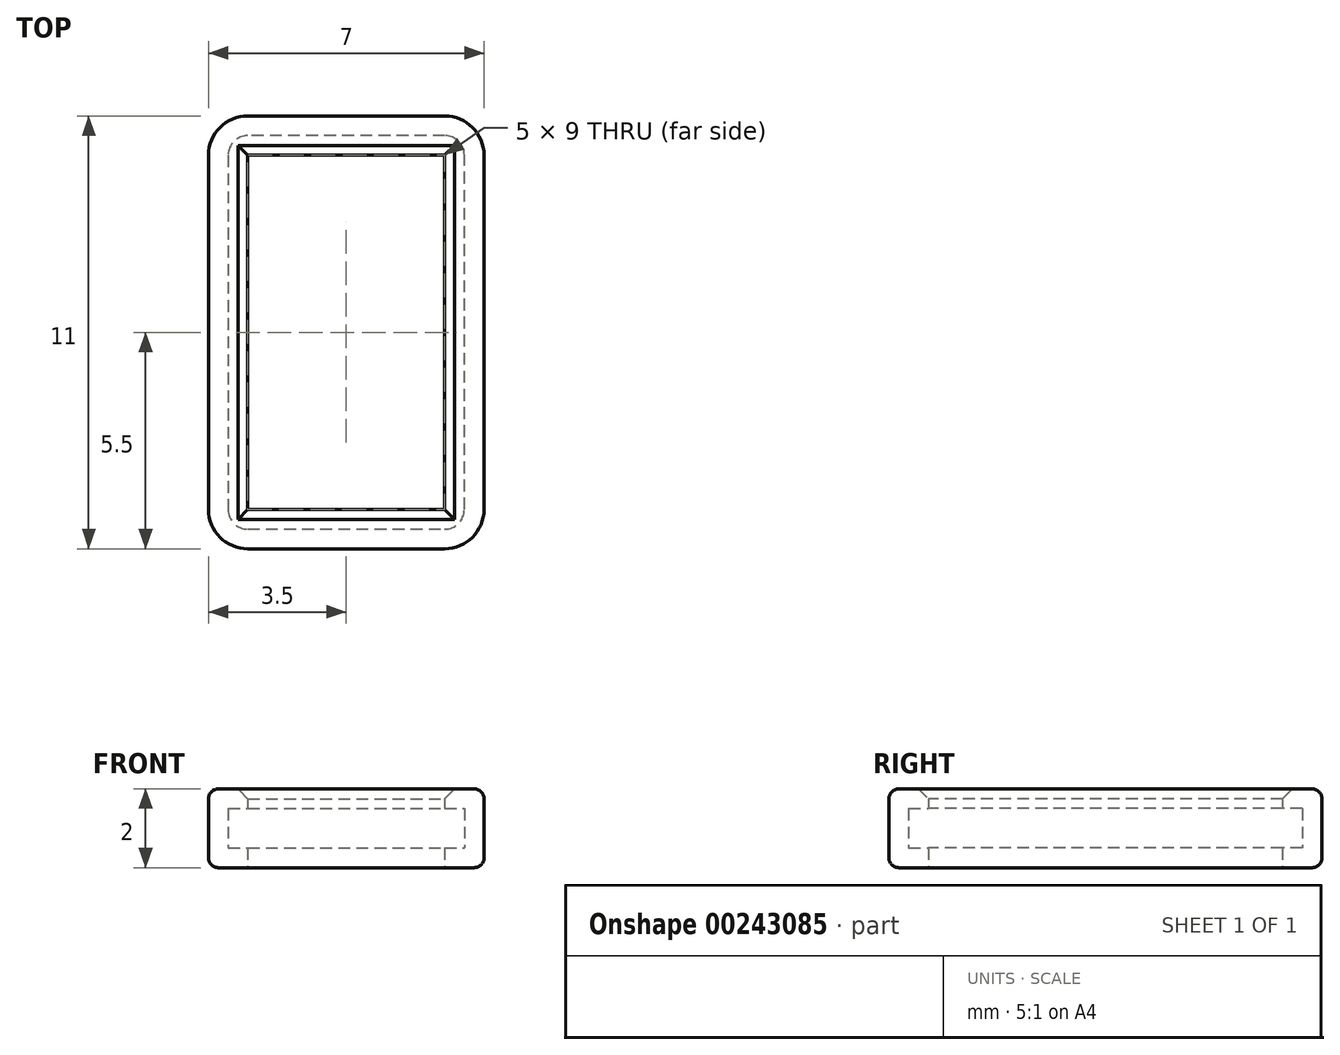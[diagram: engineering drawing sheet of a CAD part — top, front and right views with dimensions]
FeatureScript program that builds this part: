
annotation { "Feature Type Name" : "Feature", "Feature Type Description" : "" }
export const myFeature = defineFeature(function(context is Context, id is Id, definition is map)
    precondition{}
    {
        {
            var Q0;
            Q0=qCreatedBy(makeId("Top.planeOp"),FACE);
            var sketch = newSketch(context, id + "F0", { "sketchPlane" : qUnion([Q0])});
            skLineSegment(sketch, "E0.bottom", {"start": v(0, 0) * mm, "end": v(6, 0) * mm});
            skLineSegment(sketch, "E0.top", {"start": v(0, 10) * mm, "end": v(6, 10) * mm});
            skLineSegment(sketch, "E0.left", {"start": v(0, 0) * mm, "end": v(0, 10) * mm});
            skLineSegment(sketch, "E0.right", {"start": v(6, 0) * mm, "end": v(6, 10) * mm});
            skSolve(sketch);
        }
        {
            var Q0;
            Q0 = qSketchRegion(id + "F0", true);
            extrude(context, id + "F1", {"entities" : qUnion([Q0]), "depth" : 1 * mm});
        }
        {
            var Q0;
            Q0=makeQuery(id+"F1.opExtrude","SWEPT_EDGE",EDGE,{"disambiguationData":[OSD([sQuery(id+"F0.wireOp",EDGE,"E0.bottom"),sQuery(id+"F0.wireOp",EDGE,"E0.right")])]});
            var Q1;
            Q1=makeQuery(id+"F1.opExtrude","SWEPT_EDGE",EDGE,{"disambiguationData":[OSD([sQuery(id+"F0.wireOp",EDGE,"E0.top"),sQuery(id+"F0.wireOp",EDGE,"E0.right")])]});
            var Q2;
            Q2=makeQuery(id+"F1.opExtrude","SWEPT_EDGE",EDGE,{"disambiguationData":[OSD([sQuery(id+"F0.wireOp",EDGE,"E0.top"),sQuery(id+"F0.wireOp",EDGE,"E0.left")])]});
            var Q3;
            Q3=makeQuery(id+"F1.opExtrude","SWEPT_EDGE",EDGE,{"disambiguationData":[OSD([sQuery(id+"F0.wireOp",EDGE,"E0.bottom"),sQuery(id+"F0.wireOp",EDGE,"E0.left")])]});
            fillet(context, id + "F2", {"entities" : qUnion([Q0, Q1, Q2, Q3]), "radius" : .5 * mm, "tangentPropagation" : true, "allowEdgeOverflow" : false});
        }
        {
            var Q0;
            Q0=qCreatedBy(makeId("Front.planeOp"),FACE);
            cPlane(context, id + "F3", {"entities" : qUnion([Q0]), "cplaneType" : CPlaneType.OFFSET, "offset" : .5 * mm, "oppositeDirection" : true, "width" : 150 * mm, "height" : 150 * mm});
        }
        {
            var Q0;
            Q0=qCreatedBy(id+"F3.planeOp",FACE);
            var sketch = newSketch(context, id + "F4", { "sketchPlane" : qUnion([Q0])});
            skPoint(sketch, "E1.0", {"position": v(6, 1) * mm});
            skPoint(sketch, "E1.1", {"position": v(6, 0) * mm});
            skPoint(sketch, "E1.2", {"position": v(5.5, 1) * mm});
            skPoint(sketch, "E1.3", {"position": v(6, 0) * mm});
            skLineSegment(sketch, "E2", {"start": v(5.5, 1) * mm, "end": v(6, 1) * mm});
            skLineSegment(sketch, "E3", {"start": v(6, 1) * mm, "end": v(6, 0) * mm});
            skLineSegment(sketch, "E4", {"start": v(6, 0) * mm, "end": v(5.5, 0) * mm});
            skLineSegment(sketch, "E5.0", {"start": v(6.5, -0.5) * mm, "end": v(5.5, -0.5) * mm});
            skLineSegment(sketch, "E5.1", {"start": v(6.5, 1.5) * mm, "end": v(6.5, -0.5) * mm});
            skLineSegment(sketch, "E5.2", {"start": v(5.5, 1.5) * mm, "end": v(6.5, 1.5) * mm});
            skLineSegment(sketch, "E6", {"start": v(5.5, 1.5) * mm, "end": v(5.5, 1) * mm});
            skLineSegment(sketch, "E7", {"start": v(5.5, 0) * mm, "end": v(5.5, -0.5) * mm});
            skSolve(sketch);
        }
        {
            var Q0;
            Q0=makeQuery(id+"F4.imprint","IMPRINT",FACE,{"disambiguationData":[TD([[makeQuery(id+"F4.imprint","IMPRINT",EDGE,{"derivedFrom":sQuery(id+"F4.wireOp",EDGE,"E2")}),1.0]])]});
            var Q1;
            Q1=makeQuery(id+"F1.opExtrude","CAP_EDGE",EDGE,{"disambiguationData":[OSD([sQuery(id+"F0.wireOp",EDGE,"E0.bottom")])],"isStart":false});
            var Q2;
            {var subQ0=sQuery(id+"F0.wireOp",EDGE,"E0.left");var subQ1=sQuery(id+"F0.wireOp",EDGE,"E0.bottom");Q2=makeQuery(id+"F2.opFillet","BLEND_EDGE",EDGE,{"blendedFrom":[makeQuery(id+"F1.opExtrude","SWEPT_EDGE",EDGE,{"disambiguationData":[OSD([subQ1,subQ0])]}),makeQuery(id+"F1.opExtrude","CAP_FACE",FACE,{"disambiguationData":[OSD([subQ1,sQuery(id+"F0.wireOp",EDGE,"E0.top"),subQ0,sQuery(id+"F0.wireOp",EDGE,"E0.right")])],"isStart":false})],"blendedInto":[makeQuery(id+"F1.opExtrude","CAP_FACE",FACE,{"disambiguationData":[OSD([subQ1,sQuery(id+"F0.wireOp",EDGE,"E0.top"),subQ0,sQuery(id+"F0.wireOp",EDGE,"E0.right")])],"isStart":false})]});}
            var Q3;
            Q3=makeQuery(id+"F1.opExtrude","CAP_EDGE",EDGE,{"disambiguationData":[OSD([sQuery(id+"F0.wireOp",EDGE,"E0.left")])],"isStart":false});
            var Q4;
            Q4=makeQuery(id+"F1.opExtrude","CAP_EDGE",EDGE,{"disambiguationData":[OSD([sQuery(id+"F0.wireOp",EDGE,"E0.top")])],"isStart":false});
            var Q5;
            {var subQ0=sQuery(id+"F0.wireOp",EDGE,"E0.left");var subQ1=sQuery(id+"F0.wireOp",EDGE,"E0.top");Q5=makeQuery(id+"F2.opFillet","BLEND_EDGE",EDGE,{"blendedFrom":[makeQuery(id+"F1.opExtrude","SWEPT_EDGE",EDGE,{"disambiguationData":[OSD([subQ1,subQ0])]}),makeQuery(id+"F1.opExtrude","CAP_FACE",FACE,{"disambiguationData":[OSD([sQuery(id+"F0.wireOp",EDGE,"E0.bottom"),subQ1,subQ0,sQuery(id+"F0.wireOp",EDGE,"E0.right")])],"isStart":false})],"blendedInto":[makeQuery(id+"F1.opExtrude","CAP_FACE",FACE,{"disambiguationData":[OSD([sQuery(id+"F0.wireOp",EDGE,"E0.bottom"),subQ1,subQ0,sQuery(id+"F0.wireOp",EDGE,"E0.right")])],"isStart":false})]});}
            var Q6;
            {var subQ0=sQuery(id+"F0.wireOp",EDGE,"E0.right");var subQ1=sQuery(id+"F0.wireOp",EDGE,"E0.top");Q6=makeQuery(id+"F2.opFillet","BLEND_EDGE",EDGE,{"blendedFrom":[makeQuery(id+"F1.opExtrude","SWEPT_EDGE",EDGE,{"disambiguationData":[OSD([subQ1,subQ0])]}),makeQuery(id+"F1.opExtrude","CAP_FACE",FACE,{"disambiguationData":[OSD([sQuery(id+"F0.wireOp",EDGE,"E0.bottom"),subQ1,sQuery(id+"F0.wireOp",EDGE,"E0.left"),subQ0])],"isStart":false})],"blendedInto":[makeQuery(id+"F1.opExtrude","CAP_FACE",FACE,{"disambiguationData":[OSD([sQuery(id+"F0.wireOp",EDGE,"E0.bottom"),subQ1,sQuery(id+"F0.wireOp",EDGE,"E0.left"),subQ0])],"isStart":false})]});}
            var Q7;
            Q7=makeQuery(id+"F1.opExtrude","CAP_EDGE",EDGE,{"disambiguationData":[OSD([sQuery(id+"F0.wireOp",EDGE,"E0.right")])],"isStart":false});
            var Q8;
            {var subQ0=sQuery(id+"F0.wireOp",EDGE,"E0.right");var subQ1=sQuery(id+"F0.wireOp",EDGE,"E0.bottom");Q8=makeQuery(id+"F2.opFillet","BLEND_EDGE",EDGE,{"blendedFrom":[makeQuery(id+"F1.opExtrude","SWEPT_EDGE",EDGE,{"disambiguationData":[OSD([subQ1,subQ0])]}),makeQuery(id+"F1.opExtrude","CAP_FACE",FACE,{"disambiguationData":[OSD([subQ1,sQuery(id+"F0.wireOp",EDGE,"E0.top"),sQuery(id+"F0.wireOp",EDGE,"E0.left"),subQ0])],"isStart":false})],"blendedInto":[makeQuery(id+"F1.opExtrude","CAP_FACE",FACE,{"disambiguationData":[OSD([subQ1,sQuery(id+"F0.wireOp",EDGE,"E0.top"),sQuery(id+"F0.wireOp",EDGE,"E0.left"),subQ0])],"isStart":false})]});}
            sweep(context, id + "F5", {"profiles" : qUnion([Q0]), "path" : qUnion([Q1, Q2, Q3, Q4, Q5, Q6, Q7, Q8])});
        }
        {
            var Q0;
            Q0=makeQuery(id+"F5.opSweep","SWEPT_EDGE",EDGE,{"disambiguationData":[OSD([sQuery(id+"F0.wireOp",EDGE,"E0.left"),sQuery(id+"F4.wireOp",EDGE,"E5.1"),sQuery(id+"F4.wireOp",EDGE,"E5.2")])]});
            var Q1;
            {var subQ0=sQuery(id+"F4.wireOp",EDGE,"E5.2");var subQ1=sQuery(id+"F4.wireOp",EDGE,"E5.1");var subQ2=sQuery(id+"F0.wireOp",EDGE,"E0.right");var subQ3=sQuery(id+"F0.wireOp",EDGE,"E0.left");var subQ4=sQuery(id+"F0.wireOp",EDGE,"E0.top");var subQ5=sQuery(id+"F0.wireOp",EDGE,"E0.bottom");Q1=makeQuery(id+"F5.opSweep","SWEPT_EDGE",EDGE,{"disambiguationData":[OSD([subQ5,subQ4,subQ3,subQ2,subQ1,subQ0]),TDD([makeQuery(id+"F2.opFillet","BLEND_EDGE",EDGE,{"blendedFrom":[makeQuery(id+"F1.opExtrude","SWEPT_EDGE",EDGE,{"disambiguationData":[OSD([subQ5,subQ3])]}),makeQuery(id+"F1.opExtrude","CAP_FACE",FACE,{"disambiguationData":[OSD([subQ5,subQ4,subQ3,subQ2])],"isStart":false})],"blendedInto":[makeQuery(id+"F1.opExtrude","CAP_FACE",FACE,{"disambiguationData":[OSD([subQ5,subQ4,subQ3,subQ2])],"isStart":false})]}),makeQuery(id+"F4.imprint","INTERSECT",VERTEX,{"derivedFrom":[subQ1,subQ0]})])]});}
            var Q2;
            Q2=makeQuery(id+"F5.opSweep","SWEPT_EDGE",EDGE,{"disambiguationData":[OSD([sQuery(id+"F0.wireOp",EDGE,"E0.bottom"),sQuery(id+"F4.wireOp",EDGE,"E5.1"),sQuery(id+"F4.wireOp",EDGE,"E5.2")])]});
            var Q3;
            {var subQ0=sQuery(id+"F4.wireOp",EDGE,"E5.2");var subQ1=sQuery(id+"F4.wireOp",EDGE,"E5.1");var subQ2=sQuery(id+"F0.wireOp",EDGE,"E0.right");var subQ3=sQuery(id+"F0.wireOp",EDGE,"E0.left");var subQ4=sQuery(id+"F0.wireOp",EDGE,"E0.top");var subQ5=sQuery(id+"F0.wireOp",EDGE,"E0.bottom");Q3=makeQuery(id+"F5.opSweep","SWEPT_EDGE",EDGE,{"disambiguationData":[OSD([subQ5,subQ4,subQ3,subQ2,subQ1,subQ0]),TDD([makeQuery(id+"F2.opFillet","BLEND_EDGE",EDGE,{"blendedFrom":[makeQuery(id+"F1.opExtrude","SWEPT_EDGE",EDGE,{"disambiguationData":[OSD([subQ5,subQ2])]}),makeQuery(id+"F1.opExtrude","CAP_FACE",FACE,{"disambiguationData":[OSD([subQ5,subQ4,subQ3,subQ2])],"isStart":false})],"blendedInto":[makeQuery(id+"F1.opExtrude","CAP_FACE",FACE,{"disambiguationData":[OSD([subQ5,subQ4,subQ3,subQ2])],"isStart":false})]}),makeQuery(id+"F4.imprint","INTERSECT",VERTEX,{"derivedFrom":[subQ1,subQ0]})])]});}
            var Q4;
            Q4=makeQuery(id+"F5.opSweep","SWEPT_EDGE",EDGE,{"disambiguationData":[OSD([sQuery(id+"F0.wireOp",EDGE,"E0.right"),sQuery(id+"F4.wireOp",EDGE,"E5.1"),sQuery(id+"F4.wireOp",EDGE,"E5.2")])]});
            var Q5;
            {var subQ0=sQuery(id+"F4.wireOp",EDGE,"E5.2");var subQ1=sQuery(id+"F4.wireOp",EDGE,"E5.1");var subQ2=sQuery(id+"F0.wireOp",EDGE,"E0.right");var subQ3=sQuery(id+"F0.wireOp",EDGE,"E0.left");var subQ4=sQuery(id+"F0.wireOp",EDGE,"E0.top");var subQ5=sQuery(id+"F0.wireOp",EDGE,"E0.bottom");Q5=makeQuery(id+"F5.opSweep","SWEPT_EDGE",EDGE,{"disambiguationData":[OSD([subQ5,subQ4,subQ3,subQ2,subQ1,subQ0]),TDD([makeQuery(id+"F2.opFillet","BLEND_EDGE",EDGE,{"blendedFrom":[makeQuery(id+"F1.opExtrude","SWEPT_EDGE",EDGE,{"disambiguationData":[OSD([subQ4,subQ2])]}),makeQuery(id+"F1.opExtrude","CAP_FACE",FACE,{"disambiguationData":[OSD([subQ5,subQ4,subQ3,subQ2])],"isStart":false})],"blendedInto":[makeQuery(id+"F1.opExtrude","CAP_FACE",FACE,{"disambiguationData":[OSD([subQ5,subQ4,subQ3,subQ2])],"isStart":false})]}),makeQuery(id+"F4.imprint","INTERSECT",VERTEX,{"derivedFrom":[subQ1,subQ0]})])]});}
            var Q6;
            Q6=makeQuery(id+"F5.opSweep","SWEPT_EDGE",EDGE,{"disambiguationData":[OSD([sQuery(id+"F0.wireOp",EDGE,"E0.top"),sQuery(id+"F4.wireOp",EDGE,"E5.1"),sQuery(id+"F4.wireOp",EDGE,"E5.2")])]});
            var Q7;
            {var subQ0=sQuery(id+"F4.wireOp",EDGE,"E5.2");var subQ1=sQuery(id+"F4.wireOp",EDGE,"E5.1");var subQ2=sQuery(id+"F0.wireOp",EDGE,"E0.right");var subQ3=sQuery(id+"F0.wireOp",EDGE,"E0.left");var subQ4=sQuery(id+"F0.wireOp",EDGE,"E0.top");var subQ5=sQuery(id+"F0.wireOp",EDGE,"E0.bottom");Q7=makeQuery(id+"F5.opSweep","SWEPT_EDGE",EDGE,{"disambiguationData":[OSD([subQ5,subQ4,subQ3,subQ2,subQ1,subQ0]),TDD([makeQuery(id+"F2.opFillet","BLEND_EDGE",EDGE,{"blendedFrom":[makeQuery(id+"F1.opExtrude","SWEPT_EDGE",EDGE,{"disambiguationData":[OSD([subQ4,subQ3])]}),makeQuery(id+"F1.opExtrude","CAP_FACE",FACE,{"disambiguationData":[OSD([subQ5,subQ4,subQ3,subQ2])],"isStart":false})],"blendedInto":[makeQuery(id+"F1.opExtrude","CAP_FACE",FACE,{"disambiguationData":[OSD([subQ5,subQ4,subQ3,subQ2])],"isStart":false})]}),makeQuery(id+"F4.imprint","INTERSECT",VERTEX,{"derivedFrom":[subQ1,subQ0]})])]});}
            var Q8;
            Q8=makeQuery(id+"F5.opSweep","SWEPT_EDGE",EDGE,{"disambiguationData":[OSD([sQuery(id+"F0.wireOp",EDGE,"E0.bottom"),sQuery(id+"F4.wireOp",EDGE,"E5.0"),sQuery(id+"F4.wireOp",EDGE,"E5.1")])]});
            fillet(context, id + "F6", {"entities" : qUnion([Q0, Q1, Q2, Q3, Q4, Q5, Q6, Q7, Q8]), "radius" : .25 * mm, "tangentPropagation" : true, "allowEdgeOverflow" : false});
        }
        {
            var Q0;
            Q0=makeQuery(id+"F5.opSweep","SWEPT_EDGE",EDGE,{"disambiguationData":[OSD([sQuery(id+"F0.wireOp",EDGE,"E0.left"),sQuery(id+"F4.wireOp",EDGE,"E5.2"),sQuery(id+"F4.wireOp",EDGE,"E6")])]});
            var Q1;
            Q1=makeQuery(id+"F5.opSweep","SWEPT_EDGE",EDGE,{"disambiguationData":[OSD([sQuery(id+"F0.wireOp",EDGE,"E0.top"),sQuery(id+"F4.wireOp",EDGE,"E5.2"),sQuery(id+"F4.wireOp",EDGE,"E6")])]});
            var Q2;
            Q2=makeQuery(id+"F5.opSweep","SWEPT_EDGE",EDGE,{"disambiguationData":[OSD([sQuery(id+"F0.wireOp",EDGE,"E0.right"),sQuery(id+"F4.wireOp",EDGE,"E5.2"),sQuery(id+"F4.wireOp",EDGE,"E6")])]});
            var Q3;
            Q3=makeQuery(id+"F5.opSweep","SWEPT_EDGE",EDGE,{"disambiguationData":[OSD([sQuery(id+"F0.wireOp",EDGE,"E0.bottom"),sQuery(id+"F4.wireOp",EDGE,"E5.2"),sQuery(id+"F4.wireOp",EDGE,"E6")])]});
            chamfer(context, id + "F7", {"entities" : qUnion([Q0, Q1, Q2, Q3]), "chamferType" : ChamferType.TWO_OFFSETS, "width1" : .25 * mm, "oppositeDirection" : false, "width2" : .25 * mm, "tangentPropagation" : true});
        }
    });
